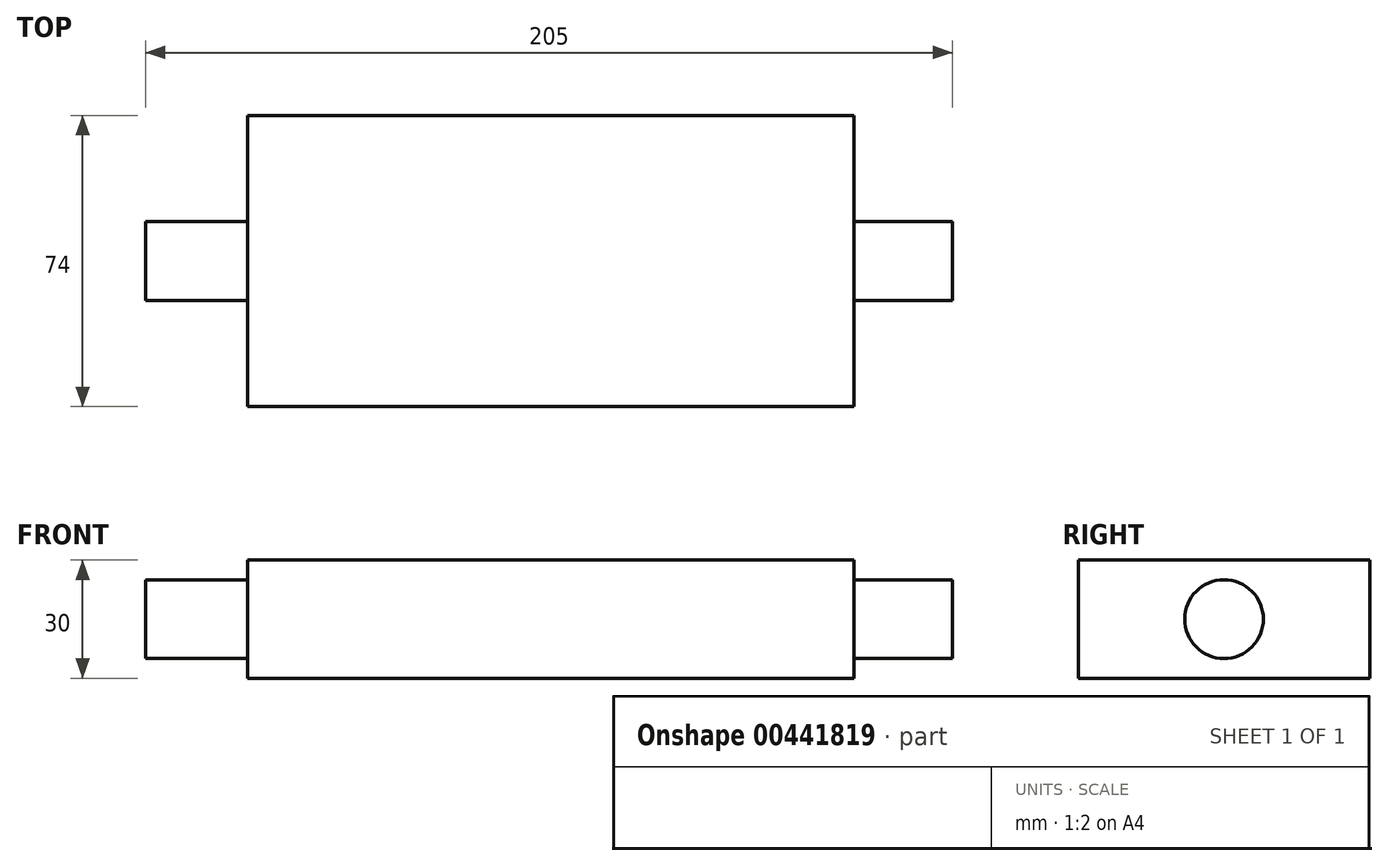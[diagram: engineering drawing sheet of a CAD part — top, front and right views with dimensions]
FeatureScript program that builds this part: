
annotation { "Feature Type Name" : "Feature", "Feature Type Description" : "" }
export const myFeature = defineFeature(function(context is Context, id is Id, definition is map)
    precondition{}
    {
        {
            var Q0;
            Q0=qCreatedBy(makeId("Top.planeOp"),FACE);
            var sketch = newSketch(context, id + "F0", { "sketchPlane" : qUnion([Q0])});
            skLineSegment(sketch, "E0.bottom", {"start": v(77, 37) * mm, "end": v(-77, 37) * mm});
            skLineSegment(sketch, "E0.top", {"start": v(77, -37) * mm, "end": v(-77, -37) * mm});
            skLineSegment(sketch, "E0.left", {"start": v(77, 37) * mm, "end": v(77, -37) * mm});
            skLineSegment(sketch, "E0.right", {"start": v(-77, 37) * mm, "end": v(-77, -37) * mm});
            skPoint(sketch, "E0.middle", {"position": v(0, 0) * mm});
            skSolve(sketch);
        }
        {
            var Q0;
            Q0=qSketchRegion(id+"F0",true);
            extrude(context, id + "F1", {"entities" : qUnion([Q0]), "depth" : 30 * mm});
        }
        {
            var Q0;
            Q0=makeQuery(id+"F1.opExtrude","SWEPT_FACE",FACE,{"disambiguationData":[OSD([sQuery(id+"F0.wireOp",EDGE,"E0.left")])]});
            var sketch = newSketch(context, id + "F2", { "sketchPlane" : qUnion([Q0])});
            skCircle(sketch, "E1", {"center": v(0, 15) * mm, "radius": 10 * mm});
            skPoint(sketch, "E1.centerSnap0", {"position": v(37, 15) * mm});
            skSolve(sketch);
        }
        {
            var Q0;
            Q0=qSketchRegion(id+"F2",true);
            extrude(context, id + "F3", {"entities" : qUnion([Q0]), "operationType" : NewBodyOperationType.ADD, "oppositeDirection" : true, "depth" : 180 * mm, "hasSecondDirection" : true, "secondDirectionOppositeDirection" : false, "secondDirectionDepth" : 25 * mm});
        }
    });
